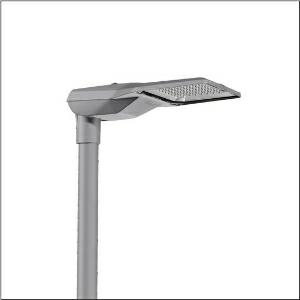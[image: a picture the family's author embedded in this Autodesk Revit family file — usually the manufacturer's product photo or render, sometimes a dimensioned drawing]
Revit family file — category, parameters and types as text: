
# Revit family: streetlight_sl_21_midi___pc-r_5xe3g43s08mb_dfdb
name_source: partatom
category: Lighting Fixtures
units: mm (PartAtom-declared; Revit-internal decimal feet)

## family parameters
Cut with Voids When Loaded = No
Host = Face
Light Source = No
Part Type = Normal
Room Calculation Point = No
Round Connector Dimension = Use Diameter
Shared = No

## types (1)
- --- (1 x LED, 19200 lm, 147 W, 4000K)
    Apparent Load = 147 VA
    CIE Flux Codes = 38 78 98 100 100
    Color Rendering = 70
    Color Temperature = 4000K
    Default Elevation = 1800 mm
    Description = Streetlight SL 21 midi, mast luminaire, primary light control with lens, of PMMA, primary optical cover: cover, of toughened safety glass, transparent, light distribution: PC-R, light emission: direct distribution, primary light characteristic: asymmetric, right, installation type: side-entry, post-top, LED, High Power LED, rated luminous flux: 19.200lm, luminous efficacy: 131lm/W, light colour: 740, colour temperature: 4000K, control gear: D4i, control: overheat protection, constant luminous flux control, time-dependent luminous flux control, flexible luminous flux parameterisation, pre-setting: logarithmic dimming characteristic, mains connection: 230..240V, AC, 50/60Hz, start of lifetime: 147W, end of service life: 155W, reduction: 65W, luminaire housing, of diecast aluminium, powder-coated, Siteco® metallic grey (DB 702S), corrosivity category C5 mid according to DIN EN ISO 12944, please order mast flange separately, inclination adjustable: 0°, 5°, 10°, 15°, sealing non-destructively replaceable, multi-level sealing system, length: 644mm, width: 335mm, height: 110mm, mast flange for spigot size: 42mm (side-entry): 5XC10008XM4, 60/48mm (side-entry/post-top): 5XC10108XM2, 76/60mm (side-entry/post-top): 5XC10108XM1, mounting height: 4..8m, Smart Interface above, protection rating (complete): IP66, insulation class (complete): insulation class II (safety insulation), certification: CE, ENEC, ENEC+, VDE, impact resistance: IK10, permissible operating ambient temperature for outdoor applications: -40..+50°C, standard-compliant lighting for roads and squares, packaging unit: 1 piece

Light Distribution: PC-R
    Height = 111 mm
    Lamp = 1 x LED
    Lamp Light Flux = 19200 lm
    Lamp Power = 147 W
    Lamp count = 1
    Length = 644 mm
    Luminous efficacy = 131 lm/W
    Manufacturer = Siteco
    ModVariant = No
    Model = 5XE3G43S08MB
    Number of Poles = 1
    OnlyDefault = Yes
    Power Factor = 1
    Product Name = Streetlight SL 21 midi | PC-R
    Product group = mast luminaire | pylon top
    ProductGroupID = 6100
    Protection Class = Protection class II
    Protection Degree = IP 66
    RLX_Detail_Level = 1
    RLX_Emergency_Light_Flux = 0 lm
    RLX_Emergency_Type = 0
    RLX_Emergency_Type_DB = No
    RlxData = <blob elided: 29401 chars, md5=cdbf4c3f>
    Socket = socket
    Standby Power = 0 W
    System Light Flux = 19200 lm
    System Power = 147 W
    Type Comments = factory setting: luminous flux: 100 % | dim-lin: 254 | 750 mA
    Type Image = l_1004302.jpg
    URL = http://relux.com
    VarID = @adj_085383
    Voltage = 0 V
    Weight = 0.00 kg
    Width = 336 mm

## geometry (parser evidence)
native form markers: Blend x4, Sweep x9
no freeform markers — native parametric forms only
